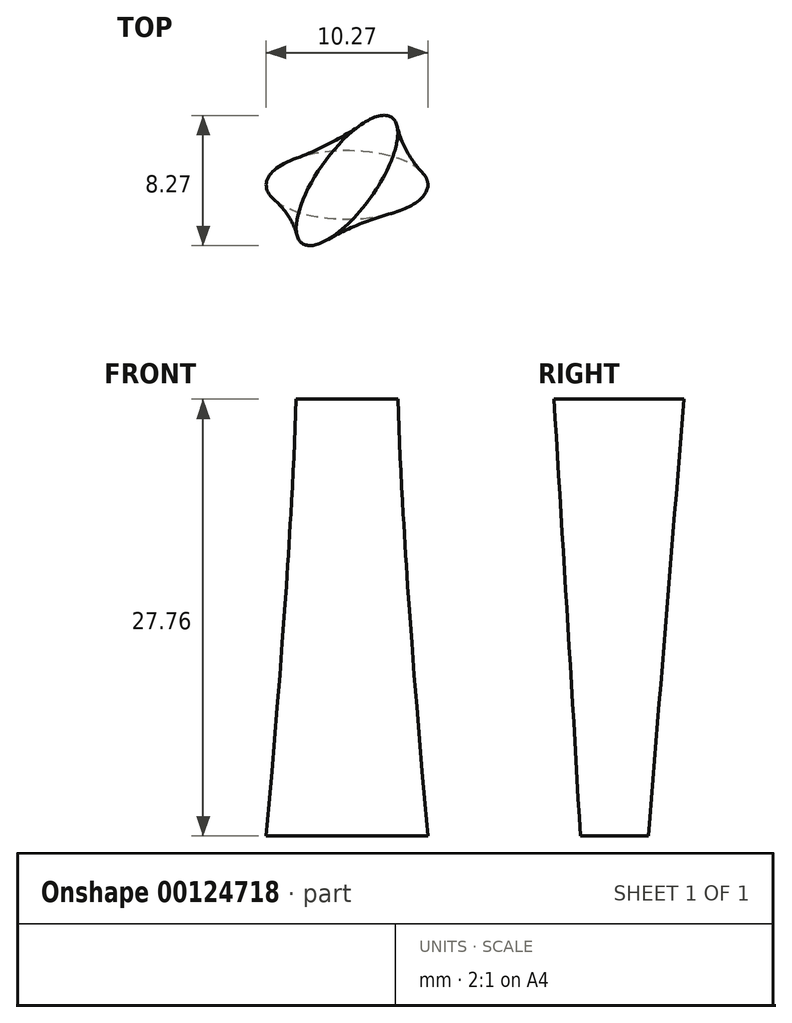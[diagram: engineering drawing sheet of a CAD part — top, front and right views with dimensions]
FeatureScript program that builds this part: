
annotation { "Feature Type Name" : "Feature", "Feature Type Description" : "" }
export const myFeature = defineFeature(function(context is Context, id is Id, definition is map)
    precondition{}
    {
        {
            var Q0;
            Q0=qCreatedBy(makeId("Top.planeOp"),FACE);
            cPlane(context, id + "F0", {"entities" : qUnion([Q0]), "cplaneType" : CPlaneType.OFFSET, "offset" : 27.76 * mm, "width" : 152.4 * mm, "height" : 152.4 * mm});
        }
        {
            var Q0;
            Q0=qCreatedBy(makeId("Top.planeOp"),FACE);
            var sketch = newSketch(context, id + "F1", { "sketchPlane" : qUnion([Q0])});
            skEllipse(sketch, "E0", {"center": v(-53.63, -28.1) * mm, "majorRadius": 5.13 * mm, "minorRadius": 2.17 * mm, "majorAxis": v(1, 0)});
            skSolve(sketch);
        }
        {
            var Q0;
            Q0=qCreatedBy(id+"F0.planeOp",FACE);
            var sketch = newSketch(context, id + "F2", { "sketchPlane" : qUnion([Q0])});
            skEllipse(sketch, "E1", {"center": v(-53.63, -27.81) * mm, "majorRadius": 4.9 * mm, "minorRadius": 1.85 * mm, "majorAxis": v(0.58, 0.81)});
            skSolve(sketch);
        }
        {
            var Q0;
            Q0=qSketchRegion(id+"F1",true);
            var Q1;
            Q1=qSketchRegion(id+"F2",true);
            loft(context, id + "F3", {"sheetProfilesArray" : [{ "sheetProfileEntities" : qUnion([Q0]) }, { "sheetProfileEntities" : qUnion([Q1]) }]});
        }
    });
